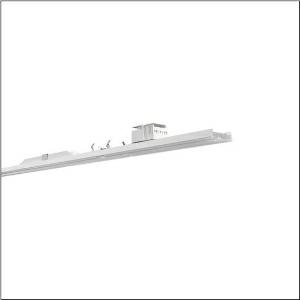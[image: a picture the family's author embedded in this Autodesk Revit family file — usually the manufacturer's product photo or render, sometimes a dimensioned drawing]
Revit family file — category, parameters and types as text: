
# Revit family: licross_r__11_recessed_ho_51tl11cn4cxr_6e9d
name_source: partatom
category: Lighting Fixtures
units: mm (PartAtom-declared; Revit-internal decimal feet)

## family parameters
Cut with Voids When Loaded = No
Host = Face
Light Source = No
Part Type = Normal
Room Calculation Point = No
Round Connector Dimension = Use Diameter
Shared = No

## types (1)
- --- (1 x LED, 12100 lm, 68.8 W, 4000K)
    Apparent Load = 69 VA
    CIE Flux Codes = 87 95 99 100 100
    Color Rendering = 80
    Color Temperature = 4000K
    Default Elevation = 1800 mm
    Description = Licross® 11 Recessed HOluminaire insert, length: 1.500mm, width: 66mm, height: 67mm, LED rated luminous flux: 12.100lm, light colour: 840, control gear: ON/OFF Multilumen, CLOi, control gear: ECG Multilumen, with plug, 3-pole, with phase selection, mains connection: 220..240V, AC, 50/60Hz, halogen-free wiring, primary optical cover: cover, of PMMA, light emission: direct distribution, protection rating (complete): IP40, insulation class (complete): insulation class I (protective earthing), certification: CE, ENEC, VDE, protection symbol: D if used in an environment without relevant dust loads with corresponding accessories, permissible ambient temperature for indoor applications: -35..+35°C, reducing of maximum allowable ambient temperature of 5°C with ceiling mounting, corresponds to IFS (International Featured Standards) requirements for safety and quality in the food industry, packaging unit: 1 piece
    Height = 58 mm
    Lamp = 1 x LED
    Lamp Light Flux = 12100 lm
    Lamp Power = 68.8 W
    Lamp count = 1
    Length = 1500 mm
    Luminous efficacy = 176 lm/W
    Manufacturer = Siteco
    ModVariant = No
    Model = 51TL11CN4CXR
    Mounting Place = Ceiling
    Mounting Type = Pendant
    Number of Poles = 1
    OnlyDefault = Yes
    Power Factor = 1
    Product Name = Licross® 11 Recessed HO
    Product group = luminaire insert
    ProductGroupID = 902
    Protection Class = Protection class I
    Protection Degree = IP 40
    RLX_Detail_Level = 1
    RlxData = <blob elided: 20057 chars, md5=d123b8a4>
    Socket = socket
    Standby Power = 0 W
    System Light Flux = 12100 lm
    System Power = 69 W
    Type Comments = factory setting: luminous flux: 100 % | (A | C | E) | 160 mA
    Type Image = l_1266722.jpg
    URL = http://relux.com
    VarID = @adj_138829
    Voltage = 0 V
    Weight = 0.00 kg
    Width = 66 mm

## geometry (parser evidence)
native form markers: Blend x4, Sweep x9
no freeform markers — native parametric forms only
